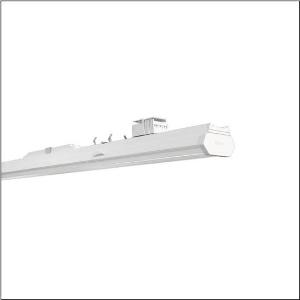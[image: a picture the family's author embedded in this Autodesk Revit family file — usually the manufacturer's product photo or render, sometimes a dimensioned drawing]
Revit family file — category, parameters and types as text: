
# Revit family: licross_r__21_protected_mo_52td12mn4a5g_9007
name_source: partatom
category: Lighting Fixtures
units: mm (PartAtom-declared; Revit-internal decimal feet)

## family parameters
Cut with Voids When Loaded = No
Host = Face
Light Source = No
Part Type = Normal
Room Calculation Point = No
Round Connector Dimension = Use Diameter
Shared = No

## types (1)
- --- (1 x LED, 10750 lm, 60.5 W, 4000K)
    Apparent Load = 61 VA
    CIE Flux Codes = 73 92 98 99 100
    Color Rendering = 80
    Color Temperature = 4000K
    Default Elevation = 1800 mm
    Description = Licross® 21 Protected MO, luminaire insert, of sheet steel, galvanised, coil coated, white, length: 1.500mm, width: 90mm, height: 101mm, LED rated luminous flux: 10.750lm, light colour: 840, control gear: ON/OFF Multilumen, with plug, 3-pole, with phase selection, mains connection: 220..240V, AC, 50/60Hz, rated input power: 61W, halogen-free wiring, primary light control with lens, of plastic, primary optical cover: cover, of PMMA, light emission: direct distribution, primary light characteristic: symmetric, protection rating (complete): IP54, insulation class (complete): insulation class I (protective earthing), certification: CE, ENEC, VDE, UKCA, protection symbol: D if used in an environment with non-conductive dust loads with corresponding accessories, impact resistance: IK06, permissible ambient temperature for indoor applications: -35..+45°C, corresponds to IFS (International Featured Standards) requirements for safety and quality in the food industry, reducing of maximum allowable ambient temperature of 5°C with ceiling mounting, LABS conformity tested according to VDMA 24364:2018-05, packaging unit: 1 piece
    Height = 92 mm
    Lamp = 1 x LED
    Lamp Light Flux = 10750 lm
    Lamp Power = 60.5 W
    Lamp count = 1
    Length = 1500 mm
    Luminous efficacy = 178 lm/W
    Manufacturer = Siteco
    ModVariant = No
    Model = 52TD12MN4A5G
    Mounting Place = Ceiling
    Mounting Type = Pendant
    Number of Poles = 1
    OnlyDefault = Yes
    Power Factor = 1
    Product Name = Licross® 21 Protected MO
    Product group = luminaire insert
    ProductGroupID = 901
    Protection Class = Protection class I
    Protection Degree = IP 54
    RLX_Detail_Level = 1
    RLX_Emergency_Light_Flux = 0 lm
    RLX_Emergency_Type = 0
    RLX_Emergency_Type_DB = No
    RlxData = <blob elided: 22033 chars, md5=7255fc49>
    Socket = socket
    Standby Power = 0 W
    System Light Flux = 10750 lm
    System Power = 61 W
    Type Comments = factory setting: luminous flux: 100 % | (A | C | E) | 140 mA
    Type Image = l_1256148.jpg
    URL = http://relux.com
    VarID = @adj_039269
    Voltage = 0 V
    Weight = 0.00 kg
    Width = 88 mm

## geometry (parser evidence)
native form markers: Blend x4, Sweep x11
no freeform markers — native parametric forms only
